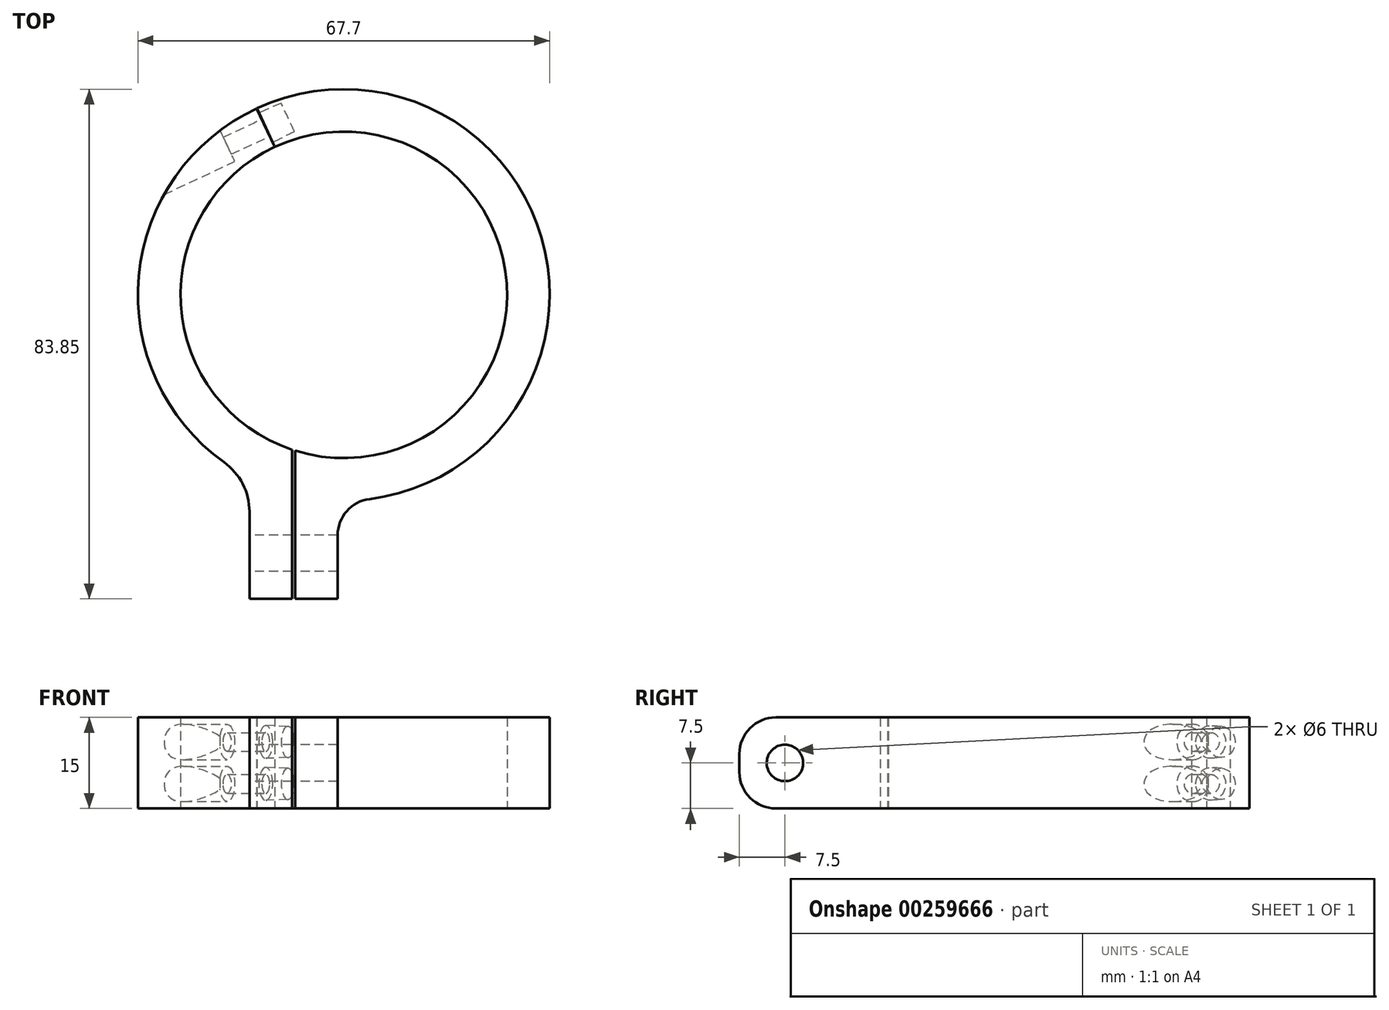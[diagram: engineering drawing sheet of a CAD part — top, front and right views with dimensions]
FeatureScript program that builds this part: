
annotation { "Feature Type Name" : "Feature", "Feature Type Description" : "" }
export const myFeature = defineFeature(function(context is Context, id is Id, definition is map)
    precondition{}
    {
        {
            var Q0;
            Q0=qCreatedBy(makeId("Top.planeOp"),FACE);
            var sketch = newSketch(context, id + "F0", { "sketchPlane" : qUnion([Q0])});
            skArc(sketch, "E0", {"start": v(-1, -33.84) * mm, "mid": v(8.46, 32.78) * mm, "end": v(-15.5, -30.1) * mm});
            skArc(sketch, "E1", {"start": v(-8, -25.63) * mm, "mid": v(8.25, 25.55) * mm, "end": v(-8.5, -25.47) * mm});
            skLineSegment(sketch, "E2.top", {"start": v(-8, -50) * mm, "end": v(-1, -50) * mm});
            skLineSegment(sketch, "E2.right", {"start": v(-1, -33.84) * mm, "end": v(-1, -50) * mm});
            skLineSegment(sketch, "E3.top", {"start": v(-8.5, -50) * mm, "end": v(-15.5, -50) * mm});
            skLineSegment(sketch, "E3.right", {"start": v(-15.5, -30.1) * mm, "end": v(-15.5, -50) * mm});
            skPoint(sketch, "E2.bottom.start.orphan", {"position": v(-8, -25.63) * mm});
            skLineSegment(sketch, "E4", {"start": v(-8, -50) * mm, "end": v(-8, -25.63) * mm});
            skLineSegment(sketch, "E5", {"start": v(-8.5, -50) * mm, "end": v(-8.5, -25.47) * mm});
            skSolve(sketch);
        }
        {
            var Q0;
            Q0=qSketchRegion(id+"F0",true);
            extrude(context, id + "F1", {"entities" : qUnion([Q0]), "depth" : 15 * mm});
        }
        {
            var Q0;
            Q0=makeQuery(id+"F1.opExtrude","CAP_EDGE",EDGE,{"disambiguationData":[OSD([sQuery(id+"F0.wireOp",EDGE,"E3.top")])],"isStart":false});
            var Q1;
            Q1=makeQuery(id+"F1.opExtrude","CAP_EDGE",EDGE,{"disambiguationData":[OSD([sQuery(id+"F0.wireOp",EDGE,"E2.top")])],"isStart":false});
            var Q2;
            Q2=makeQuery(id+"F1.opExtrude","CAP_EDGE",EDGE,{"disambiguationData":[OSD([sQuery(id+"F0.wireOp",EDGE,"E3.top")])],"isStart":true});
            var Q3;
            Q3=makeQuery(id+"F1.opExtrude","CAP_EDGE",EDGE,{"disambiguationData":[OSD([sQuery(id+"F0.wireOp",EDGE,"E2.top")])],"isStart":true});
            fillet(context, id + "F2", {"entities" : qUnion([Q0, Q1, Q2, Q3]), "radius" : 6 * mm, "tangentPropagation" : true, "allowEdgeOverflow" : false});
        }
        {
            var Q0;
            Q0=makeQuery(id+"F1.opExtrude","SWEPT_EDGE",EDGE,{"disambiguationData":[OSD([sQuery(id+"F0.wireOp",EDGE,"E0"),sQuery(id+"F0.wireOp",EDGE,"E3.right")])]});
            fillet(context, id + "F3", {"entities" : qUnion([Q0]), "radius" : 10 * mm, "tangentPropagation" : true, "allowEdgeOverflow" : false});
        }
        {
            var Q0;
            Q0=makeQuery(id+"F1.opExtrude","SWEPT_EDGE",EDGE,{"disambiguationData":[OSD([sQuery(id+"F0.wireOp",EDGE,"E0"),sQuery(id+"F0.wireOp",EDGE,"E2.right")])]});
            fillet(context, id + "F4", {"entities" : qUnion([Q0]), "radius" : 6 * mm, "tangentPropagation" : true, "allowEdgeOverflow" : false});
        }
        {
            var Q0;
            Q0=makeQuery(id+"F1.opExtrude","SWEPT_FACE",FACE,{"disambiguationData":[OSD([sQuery(id+"F0.wireOp",EDGE,"E3.right")])]});
            var sketch = newSketch(context, id + "F5", { "sketchPlane" : qUnion([Q0])});
            skCircle(sketch, "E6", {"center": v(42.5, 7.5) * mm, "radius": 3 * mm});
            skSolve(sketch);
        }
        {
            var Q0;
            Q0=qSketchRegion(id+"F5",true);
            extrude(context, id + "F6", {"entities" : qUnion([Q0]), "operationType" : NewBodyOperationType.REMOVE, "endBound" : BoundingType.THROUGH_ALL, "oppositeDirection" : true, "depth" : 25 * mm});
        }
        {
            var Q0;
            Q0=qCreatedBy(makeId("Top.planeOp"),FACE);
            var sketch = newSketch(context, id + "F7", { "sketchPlane" : qUnion([Q0])});
            skLineSegment(sketch, "E7", {"start": v(0, 0) * mm, "end": v(-15.57, 33.39) * mm});
            skLineSegment(sketch, "E8", {"start": v(0, 0) * mm, "end": v(0, 10.27) * mm, "construction": true});
            skLineSegment(sketch, "E9.0", {"start": v(0, 0) * mm, "end": v(-15.56, 33.4) * mm});
            skLineSegment(sketch, "E10", {"start": v(-15.57, 33.39) * mm, "end": v(-15.56, 33.4) * mm});
            skLineSegment(sketch, "E11", {"start": v(0, 0) * mm, "end": v(0, 0) * mm});
            skSolve(sketch);
        }
        {
            var Q0;
            Q0 = qSketchRegion(id + "F7", true);
            extrude(context, id + "F8", {"entities" : qUnion([Q0]), "operationType" : NewBodyOperationType.REMOVE, "endBound" : BoundingType.THROUGH_ALL, "depth" : 25 * mm});
        }
        {
            var Q0;
            Q0=makeQuery(id+"F8.boolean.opBoolean","COPY",FACE,{"derivedFrom":makeQuery(id+"F8.opExtrude","SWEPT_FACE",FACE,{"disambiguationData":[OSD([sQuery(id+"F7.wireOp",EDGE,"E7")])]})});
            var sketch = newSketch(context, id + "F9", { "sketchPlane" : qUnion([Q0])});
            skLineSegment(sketch, "E12", {"start": v(30.35, 15) * mm, "end": v(30.35, 0) * mm, "construction": true});
            skCircle(sketch, "E13", {"center": v(30.35, 10.95) * mm, "radius": 1.55 * mm});
            skCircle(sketch, "E14", {"center": v(30.35, 4.05) * mm, "radius": 1.55 * mm});
            skCircle(sketch, "E15", {"center": v(30.35, 10.95) * mm, "radius": 2.85 * mm, "construction": true});
            skCircle(sketch, "E16", {"center": v(30.35, 4.05) * mm, "radius": 2.85 * mm, "construction": true});
            skSolve(sketch);
        }
        {
            var Q0;
            Q0 = qSketchRegion(id + "F9", true);
            extrude(context, id + "F10", {"entities" : qUnion([Q0]), "operationType" : NewBodyOperationType.REMOVE, "oppositeDirection" : true, "depth" : 7 * mm, "hasSecondDirection" : true, "secondDirectionOppositeDirection" : false, "secondDirectionDepth" : 3.8 * mm});
        }
        {
            var Q0;
            Q0=makeQuery(id+"F8.boolean.opBoolean","COPY",FACE,{"derivedFrom":makeQuery(id+"F8.opExtrude","SWEPT_FACE",FACE,{"disambiguationData":[OSD([sQuery(id+"F7.wireOp",EDGE,"E9.0")])]})});
            var sketch = newSketch(context, id + "F11", { "sketchPlane" : qUnion([Q0])});
            skCircle(sketch, "E17", {"center": v(-30.35, 10.95) * mm, "radius": 2.7 * mm});
            skCircle(sketch, "E18", {"center": v(-30.35, 4.05) * mm, "radius": 2.7 * mm});
            skSolve(sketch);
        }
        {
            var Q0;
            Q0 = qSketchRegion(id + "F11", true);
            extrude(context, id + "F12", {"entities" : qUnion([Q0]), "operationType" : NewBodyOperationType.REMOVE, "oppositeDirection" : true, "depth" : 4 * mm, "hasDraft" : true, "draftAngle" : 2 * degree, "draftPullDirection" : true});
        }
        {
            var Q0;
            Q0=makeQuery(id+"F10.boolean.opBoolean","COPY",FACE,{"derivedFrom":makeQuery(id+"F10.opExtrude","CAP_FACE",FACE,{"disambiguationData":[OSD([sQuery(id+"F9.wireOp",EDGE,"E13")])],"isStart":false})});
            var sketch = newSketch(context, id + "F13", { "sketchPlane" : qUnion([Q0])});
            skCircle(sketch, "E19", {"center": v(30.35, 10.95) * mm, "radius": 2.9 * mm});
            skCircle(sketch, "E20", {"center": v(30.35, 4.05) * mm, "radius": 2.9 * mm});
            skSolve(sketch);
        }
        {
            var Q0;
            Q0 = qSketchRegion(id + "F13", true);
            extrude(context, id + "F14", {"entities" : qUnion([Q0]), "operationType" : NewBodyOperationType.REMOVE, "endBound" : BoundingType.THROUGH_ALL, "oppositeDirection" : true, "depth" : 25 * mm});
        }
    });
